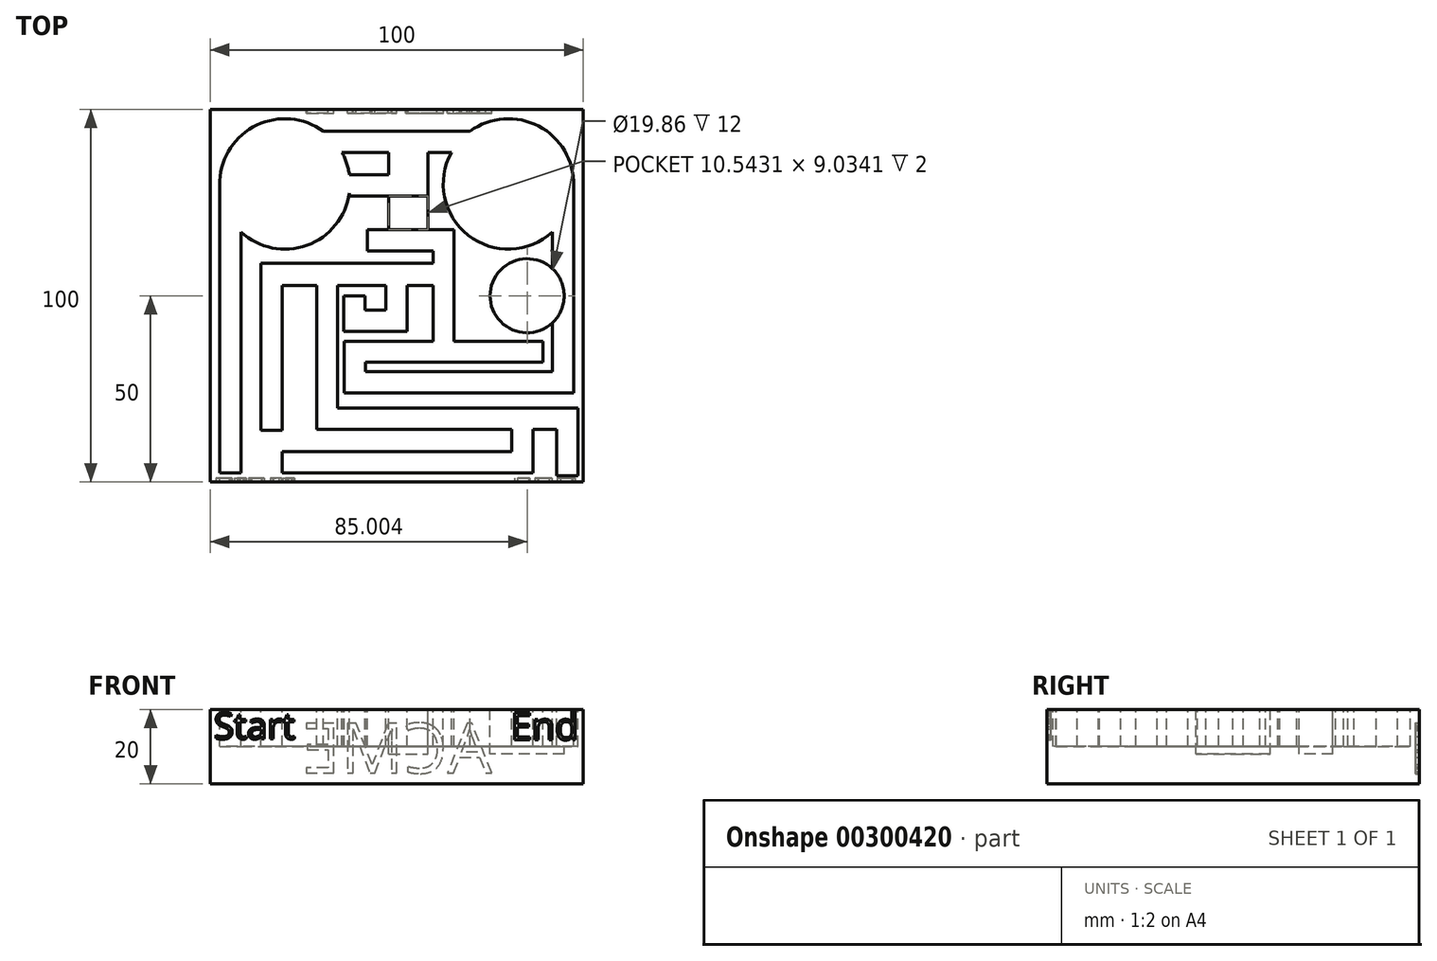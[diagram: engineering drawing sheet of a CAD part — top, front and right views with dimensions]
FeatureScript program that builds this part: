
annotation { "Feature Type Name" : "Feature", "Feature Type Description" : "" }
export const myFeature = defineFeature(function(context is Context, id is Id, definition is map)
    precondition{}
    {
        {
            var Q0;
            Q0=qCreatedBy(makeId("Top.planeOp"),FACE);
            var sketch = newSketch(context, id + "F0", { "sketchPlane" : qUnion([Q0])});
            skLineSegment(sketch, "E0.bottom", {"start": v(-50, 50) * mm, "end": v(50, 50) * mm});
            skLineSegment(sketch, "E0.top", {"start": v(-50, -50) * mm, "end": v(50, -50) * mm});
            skLineSegment(sketch, "E0.left", {"start": v(-50, 50) * mm, "end": v(-50, -50) * mm});
            skLineSegment(sketch, "E0.right", {"start": v(50, 50) * mm, "end": v(50, -50) * mm});
            skPoint(sketch, "E0.middle", {"position": v(0, 0) * mm});
            skSolve(sketch);
        }
        {
            var Q0;
            Q0 = qSketchRegion(id + "F0", true);
            extrude(context, id + "F1", {"entities" : qUnion([Q0]), "oppositeDirection" : true, "depth" : 20 * mm});
        }
        {
            var Q0;
            Q0=makeQuery(id+"F1.opExtrude","CAP_FACE",FACE,{"disambiguationData":[OSD([sQuery(id+"F0.wireOp",EDGE,"E0.bottom"),sQuery(id+"F0.wireOp",EDGE,"E0.top"),sQuery(id+"F0.wireOp",EDGE,"E0.left"),sQuery(id+"F0.wireOp",EDGE,"E0.right")])],"isStart":true});
            var sketch = newSketch(context, id + "F2", { "sketchPlane" : qUnion([Q0])});
            skCircle(sketch, "E1", {"center": v(-30, 30) * mm, "radius": 17.5 * mm});
            skCircle(sketch, "E2", {"center": v(30, 30) * mm, "radius": 17.5 * mm});
            skLineSegment(sketch, "E3.bottom", {"start": v(-47.5, -47.5) * mm, "end": v(-41.8, -47.5) * mm});
            skLineSegment(sketch, "E3.top", {"start": v(-47.5, 30.85) * mm, "end": v(-41.8, 30.85) * mm});
            skLineSegment(sketch, "E3.left", {"start": v(-47.5, -47.5) * mm, "end": v(-47.5, 30.85) * mm});
            skLineSegment(sketch, "E3.right", {"start": v(-41.8, -47.5) * mm, "end": v(-41.8, 30.85) * mm});
            skLineSegment(sketch, "E4.bottom", {"start": v(-19.7, 44.15) * mm, "end": v(19.87, 44.15) * mm});
            skLineSegment(sketch, "E4.top", {"start": v(-19.7, 38.45) * mm, "end": v(19.87, 38.45) * mm});
            skLineSegment(sketch, "E4.left", {"start": v(-19.7, 44.15) * mm, "end": v(-19.7, 38.45) * mm});
            skLineSegment(sketch, "E4.right", {"start": v(19.87, 44.15) * mm, "end": v(19.87, 38.45) * mm});
            skLineSegment(sketch, "E5.bottom", {"start": v(-12.68, 32.47) * mm, "end": v(8.37, 32.47) * mm});
            skLineSegment(sketch, "E5.top", {"start": v(-12.68, 26.77) * mm, "end": v(8.37, 26.77) * mm});
            skLineSegment(sketch, "E5.left", {"start": v(-12.68, 32.47) * mm, "end": v(-12.68, 26.77) * mm});
            skLineSegment(sketch, "E5.right", {"start": v(8.37, 32.47) * mm, "end": v(8.37, 26.77) * mm});
            skLineSegment(sketch, "E6.bottom", {"start": v(8.37, 26.77) * mm, "end": v(2.75, 26.77) * mm});
            skPoint(sketch, "E7.firstSnap0", {"position": v(-2.15, 32.47) * mm});
            skLineSegment(sketch, "E7.bottom", {"start": v(-2.15, 38.45) * mm, "end": v(8.37, 38.45) * mm});
            skLineSegment(sketch, "E7.top", {"start": v(-2.15, 32.47) * mm, "end": v(8.37, 32.47) * mm});
            skLineSegment(sketch, "E7.left", {"start": v(-2.15, 38.45) * mm, "end": v(-2.15, 32.47) * mm});
            skLineSegment(sketch, "E7.right", {"start": v(8.37, 38.45) * mm, "end": v(8.37, 32.47) * mm});
            skPoint(sketch, "E8.firstSnap0", {"position": v(8.37, 29.62) * mm});
            skLineSegment(sketch, "E8.bottom", {"start": v(41.8, 29.62) * mm, "end": v(47.5, 29.62) * mm});
            skLineSegment(sketch, "E8.top", {"start": v(41.8, -0.23) * mm, "end": v(47.5, -0.23) * mm});
            skLineSegment(sketch, "E8.left", {"start": v(47.5, 29.62) * mm, "end": v(47.5, -0.23) * mm});
            skLineSegment(sketch, "E8.right", {"start": v(41.8, 29.62) * mm, "end": v(41.8, -0.23) * mm});
            skPoint(sketch, "E9.oppositeSnap0", {"position": v(50, 0) * mm});
            skLineSegment(sketch, "E10.right", {"start": v(-41.8, 7.74) * mm, "end": v(-41.8, 2.93) * mm});
            skLineSegment(sketch, "E11.bottom", {"start": v(47.5, -0.23) * mm, "end": v(41.8, -0.23) * mm});
            skLineSegment(sketch, "E11.top", {"start": v(47.5, -26.08) * mm, "end": v(41.8, -26.08) * mm});
            skLineSegment(sketch, "E11.left", {"start": v(47.5, -0.23) * mm, "end": v(47.5, -26.08) * mm});
            skLineSegment(sketch, "E11.right", {"start": v(41.8, -0.23) * mm, "end": v(41.8, -26.08) * mm});
            skLineSegment(sketch, "E12.bottom", {"start": v(41.8, -26.08) * mm, "end": v(-14.13, -26.08) * mm});
            skLineSegment(sketch, "E12.top", {"start": v(41.8, -20.38) * mm, "end": v(-14.13, -20.38) * mm});
            skLineSegment(sketch, "E12.left", {"start": v(41.8, -26.08) * mm, "end": v(41.8, -20.38) * mm});
            skLineSegment(sketch, "E12.right", {"start": v(-14.13, -26.08) * mm, "end": v(-14.13, -20.38) * mm});
            skLineSegment(sketch, "E13.bottom", {"start": v(-14.13, -20.38) * mm, "end": v(-8.43, -20.38) * mm});
            skLineSegment(sketch, "E13.top", {"start": v(-14.13, -12.18) * mm, "end": v(-8.43, -12.18) * mm});
            skLineSegment(sketch, "E13.left", {"start": v(-14.13, -20.38) * mm, "end": v(-14.13, -12.18) * mm});
            skLineSegment(sketch, "E13.right", {"start": v(-8.43, -20.38) * mm, "end": v(-8.43, -12.18) * mm});
            skLineSegment(sketch, "E14.bottom", {"start": v(-8.43, -12.18) * mm, "end": v(39.3, -12.18) * mm});
            skLineSegment(sketch, "E14.top", {"start": v(-8.43, -17.88) * mm, "end": v(39.3, -17.88) * mm});
            skLineSegment(sketch, "E14.left", {"start": v(-8.43, -12.18) * mm, "end": v(-8.43, -17.88) * mm});
            skLineSegment(sketch, "E14.right", {"start": v(39.3, -12.18) * mm, "end": v(39.3, -17.88) * mm});
            skLineSegment(sketch, "E15.bottom", {"start": v(39.3, -12.18) * mm, "end": v(32.77, -12.18) * mm});
            skLineSegment(sketch, "E15.top", {"start": v(39.3, -12.18) * mm, "end": v(32.77, -12.18) * mm});
            skLineSegment(sketch, "E15.left", {"start": v(39.3, -12.18) * mm, "end": v(39.3, -12.18) * mm});
            skLineSegment(sketch, "E15.right", {"start": v(32.77, -12.18) * mm, "end": v(32.77, -12.18) * mm});
            skLineSegment(sketch, "E16.bottom", {"start": v(15.43, -12.18) * mm, "end": v(9.73, -12.18) * mm});
            skLineSegment(sketch, "E16.top", {"start": v(15.43, 17.74) * mm, "end": v(9.73, 17.74) * mm});
            skLineSegment(sketch, "E16.left", {"start": v(15.43, -12.18) * mm, "end": v(15.43, 17.74) * mm});
            skLineSegment(sketch, "E16.right", {"start": v(9.73, -12.18) * mm, "end": v(9.73, 17.74) * mm});
            skLineSegment(sketch, "E17.bottom", {"start": v(9.73, 17.74) * mm, "end": v(-7.9, 17.74) * mm});
            skLineSegment(sketch, "E17.top", {"start": v(9.73, 12.04) * mm, "end": v(-7.9, 12.04) * mm});
            skLineSegment(sketch, "E17.left", {"start": v(9.73, 17.74) * mm, "end": v(9.73, 12.04) * mm});
            skLineSegment(sketch, "E17.right", {"start": v(-7.9, 17.74) * mm, "end": v(-7.9, 12.04) * mm});
            skPoint(sketch, "E18.oppositeSnap0", {"position": v(9.73, 2.78) * mm});
            skLineSegment(sketch, "E18.bottom", {"start": v(9.73, 8.7) * mm, "end": v(-36.49, 8.7) * mm});
            skLineSegment(sketch, "E18.top", {"start": v(9.73, 2.78) * mm, "end": v(-36.49, 2.78) * mm});
            skLineSegment(sketch, "E18.left", {"start": v(9.73, 8.7) * mm, "end": v(9.73, 2.78) * mm});
            skLineSegment(sketch, "E18.right", {"start": v(-36.49, 8.7) * mm, "end": v(-36.49, 2.78) * mm});
            skLineSegment(sketch, "E19.bottom", {"start": v(2.85, 2.78) * mm, "end": v(-2.85, 2.78) * mm});
            skLineSegment(sketch, "E19.top", {"start": v(2.85, -9.53) * mm, "end": v(-2.85, -9.53) * mm});
            skLineSegment(sketch, "E19.left", {"start": v(2.85, 2.78) * mm, "end": v(2.85, -9.53) * mm});
            skLineSegment(sketch, "E19.right", {"start": v(-2.85, 2.78) * mm, "end": v(-2.85, -9.53) * mm});
            skLineSegment(sketch, "E20.bottom", {"start": v(-2.85, -9.53) * mm, "end": v(-14.25, -9.53) * mm});
            skLineSegment(sketch, "E20.top", {"start": v(-2.85, -3.83) * mm, "end": v(-14.25, -3.83) * mm});
            skLineSegment(sketch, "E20.left", {"start": v(-2.85, -9.53) * mm, "end": v(-2.85, -3.83) * mm});
            skLineSegment(sketch, "E20.right", {"start": v(-14.25, -9.53) * mm, "end": v(-14.25, -3.83) * mm});
            skPoint(sketch, "E21.oppositeSnap0", {"position": v(-8.55, -3.83) * mm});
            skLineSegment(sketch, "E21.bottom", {"start": v(-14.25, -3.83) * mm, "end": v(-8.55, -3.83) * mm});
            skLineSegment(sketch, "E21.top", {"start": v(-14.25, 0) * mm, "end": v(-8.55, 0) * mm});
            skLineSegment(sketch, "E21.left", {"start": v(-14.25, -3.83) * mm, "end": v(-14.25, 0) * mm});
            skLineSegment(sketch, "E21.right", {"start": v(-8.55, -3.83) * mm, "end": v(-8.55, 0) * mm});
            skLineSegment(sketch, "E22.bottom", {"start": v(-15.81, 2.78) * mm, "end": v(-21.51, 2.78) * mm});
            skLineSegment(sketch, "E22.top", {"start": v(-15.81, -25.97) * mm, "end": v(-21.51, -25.97) * mm});
            skLineSegment(sketch, "E22.left", {"start": v(-15.81, 2.78) * mm, "end": v(-15.81, -25.97) * mm});
            skLineSegment(sketch, "E22.right", {"start": v(-21.51, 2.78) * mm, "end": v(-21.51, -25.97) * mm});
            skLineSegment(sketch, "E23.bottom", {"start": v(-21.51, -25.97) * mm, "end": v(-15.81, -25.97) * mm});
            skLineSegment(sketch, "E23.top", {"start": v(-21.51, -35.9) * mm, "end": v(-15.81, -35.9) * mm});
            skLineSegment(sketch, "E23.left", {"start": v(-21.51, -25.97) * mm, "end": v(-21.51, -35.9) * mm});
            skLineSegment(sketch, "E23.right", {"start": v(-15.81, -25.97) * mm, "end": v(-15.81, -35.9) * mm});
            skLineSegment(sketch, "E24.bottom", {"start": v(-15.81, -35.9) * mm, "end": v(48.6, -35.9) * mm});
            skLineSegment(sketch, "E24.top", {"start": v(-15.81, -30.2) * mm, "end": v(48.6, -30.2) * mm});
            skLineSegment(sketch, "E24.left", {"start": v(-15.81, -35.9) * mm, "end": v(-15.81, -30.2) * mm});
            skLineSegment(sketch, "E24.right", {"start": v(48.6, -35.9) * mm, "end": v(48.6, -30.2) * mm});
            skLineSegment(sketch, "E25.bottom", {"start": v(48.6, -35.9) * mm, "end": v(42.9, -35.9) * mm});
            skLineSegment(sketch, "E25.top", {"start": v(48.6, -48.27) * mm, "end": v(42.9, -48.27) * mm});
            skLineSegment(sketch, "E25.left", {"start": v(48.6, -35.9) * mm, "end": v(48.6, -48.27) * mm});
            skLineSegment(sketch, "E25.right", {"start": v(42.9, -35.9) * mm, "end": v(42.9, -48.27) * mm});
            skLineSegment(sketch, "E26.bottom", {"start": v(36.53, -35.9) * mm, "end": v(30.83, -35.9) * mm});
            skLineSegment(sketch, "E26.top", {"start": v(36.53, -35.9) * mm, "end": v(30.83, -35.9) * mm});
            skLineSegment(sketch, "E26.left", {"start": v(36.53, -35.9) * mm, "end": v(36.53, -35.9) * mm});
            skLineSegment(sketch, "E26.right", {"start": v(30.83, -35.9) * mm, "end": v(30.83, -35.9) * mm});
            skLineSegment(sketch, "E27.bottom", {"start": v(-26.07, 2.78) * mm, "end": v(-29.98, 2.78) * mm});
            skLineSegment(sketch, "E28.bottom", {"start": v(-36.49, 2.78) * mm, "end": v(-30.79, 2.78) * mm});
            skLineSegment(sketch, "E28.top", {"start": v(-36.49, -36.16) * mm, "end": v(-30.79, -36.16) * mm});
            skLineSegment(sketch, "E28.left", {"start": v(-36.49, 2.78) * mm, "end": v(-36.49, -36.16) * mm});
            skLineSegment(sketch, "E28.right", {"start": v(-30.79, 2.78) * mm, "end": v(-30.79, -36.16) * mm});
            skLineSegment(sketch, "E29.top", {"start": v(36.53, -47.5) * mm, "end": v(30.83, -47.5) * mm});
            skLineSegment(sketch, "E29.left", {"start": v(36.53, -35.9) * mm, "end": v(36.53, -47.5) * mm});
            skLineSegment(sketch, "E29.right", {"start": v(30.83, -35.9) * mm, "end": v(30.83, -47.5) * mm});
            skLineSegment(sketch, "E30.bottom", {"start": v(30.83, -47.5) * mm, "end": v(-7.54, -47.5) * mm});
            skLineSegment(sketch, "E30.top", {"start": v(30.83, -41.8) * mm, "end": v(-7.54, -41.8) * mm});
            skLineSegment(sketch, "E30.left", {"start": v(30.83, -47.5) * mm, "end": v(30.83, -41.8) * mm});
            skLineSegment(sketch, "E30.right", {"start": v(-7.54, -47.5) * mm, "end": v(-7.54, -41.8) * mm});
            skLineSegment(sketch, "E31.bottom", {"start": v(-7.54, -41.8) * mm, "end": v(-30.79, -41.8) * mm});
            skLineSegment(sketch, "E31.top", {"start": v(-7.54, -47.5) * mm, "end": v(-30.79, -47.5) * mm});
            skLineSegment(sketch, "E31.left", {"start": v(-7.54, -41.8) * mm, "end": v(-7.54, -47.5) * mm});
            skLineSegment(sketch, "E31.right", {"start": v(-30.79, -41.8) * mm, "end": v(-30.79, -47.5) * mm});
            skSolve(sketch);
        }
        {
            var Q0;
            Q0 = qSketchRegion(id + "F2", true);
            extrude(context, id + "F3", {"entities" : qUnion([Q0]), "operationType" : NewBodyOperationType.REMOVE, "oppositeDirection" : true, "depth" : 10 * mm});
        }
        {
            var Q0;
            {var subQ18=sQuery(id+"F0.wireOp",EDGE,"E0.bottom");var subQ22=sQuery(id+"F0.wireOp",EDGE,"E0.right");var subQ23=sQuery(id+"F0.wireOp",EDGE,"E0.top");var subQ24=sQuery(id+"F0.wireOp",EDGE,"E0.left");Q0=makeQuery(id+"F3.boolean.opBoolean","SPLIT",FACE,{"disambiguationData":[TD([makeQuery(id+"F1.opExtrude","SWEPT_FACE",FACE,{"disambiguationData":[OSD([subQ18])]})])],"derivedFrom":makeQuery(id+"F1.opExtrude","CAP_FACE",FACE,{"disambiguationData":[OSD([subQ18,subQ23,subQ24,subQ22])],"isStart":true})});}
            var sketch = newSketch(context, id + "F4", { "sketchPlane" : qUnion([Q0])});
            skCircle(sketch, "E32", {"center": v(35, 0) * mm, "radius": 9.93 * mm});
            skLineSegment(sketch, "E33.bottom", {"start": v(-2.15, 26.77) * mm, "end": v(8.4, 26.77) * mm});
            skLineSegment(sketch, "E33.top", {"start": v(-2.15, 17.74) * mm, "end": v(8.4, 17.74) * mm});
            skLineSegment(sketch, "E33.left", {"start": v(-2.15, 26.77) * mm, "end": v(-2.15, 17.74) * mm});
            skLineSegment(sketch, "E33.right", {"start": v(8.4, 26.77) * mm, "end": v(8.4, 17.74) * mm});
            skSolve(sketch);
        }
        {
            var Q0;
            Q0 = qSketchRegion(id + "F4", true);
            extrude(context, id + "F5", {"entities" : qUnion([Q0]), "operationType" : NewBodyOperationType.REMOVE, "oppositeDirection" : true, "depth" : 12 * mm});
        }
        {
            var Q0;
            Q0=makeQuery(id+"F1.opExtrude","SWEPT_FACE",FACE,{"disambiguationData":[OSD([sQuery(id+"F0.wireOp",EDGE,"E0.top")])]});
            var sketch = newSketch(context, id + "F6", { "sketchPlane" : qUnion([Q0])});
            skText(sketch, "E34", { "text": "Start\n", "fontName": "OpenSans-Regular.ttf"});
            skText(sketch, "E35", { "text": "End", "fontName": "OpenSans-Regular.ttf"});
            const initialGuessF6  = {"E34": [-0.04907, -0.00793, 1, 0, 0.00707], "E35": [0.03061, -0.00818, 1, 0, 0.00732]};
            skSetInitialGuess(sketch, initialGuessF6);
            skSolve(sketch);
        }
        {
            var Q0;
            Q0 = qSketchRegion(id + "F6", true);
            extrude(context, id + "F7", {"entities" : qUnion([Q0]), "operationType" : NewBodyOperationType.REMOVE, "oppositeDirection" : true, "depth" : 1 * mm});
        }
        {
            var Q0;
            Q0=makeQuery(id+"F1.opExtrude","SWEPT_FACE",FACE,{"disambiguationData":[OSD([sQuery(id+"F0.wireOp",EDGE,"E0.bottom")])]});
            var sketch = newSketch(context, id + "F8", { "sketchPlane" : qUnion([Q0])});
            skText(sketch, "E36", { "text": "ACME", "fontName": "OpenSans-Regular.ttf"});
            const initialGuessF8  = {"E36": [-0.02549, -0.01708, 1, 0, 0.01346]};
            skSetInitialGuess(sketch, initialGuessF8);
            skSolve(sketch);
        }
        {
            var Q0;
            Q0 = qSketchRegion(id + "F8", true);
            extrude(context, id + "F9", {"entities" : qUnion([Q0]), "operationType" : NewBodyOperationType.REMOVE, "oppositeDirection" : true, "depth" : 1 * mm});
        }
    });
